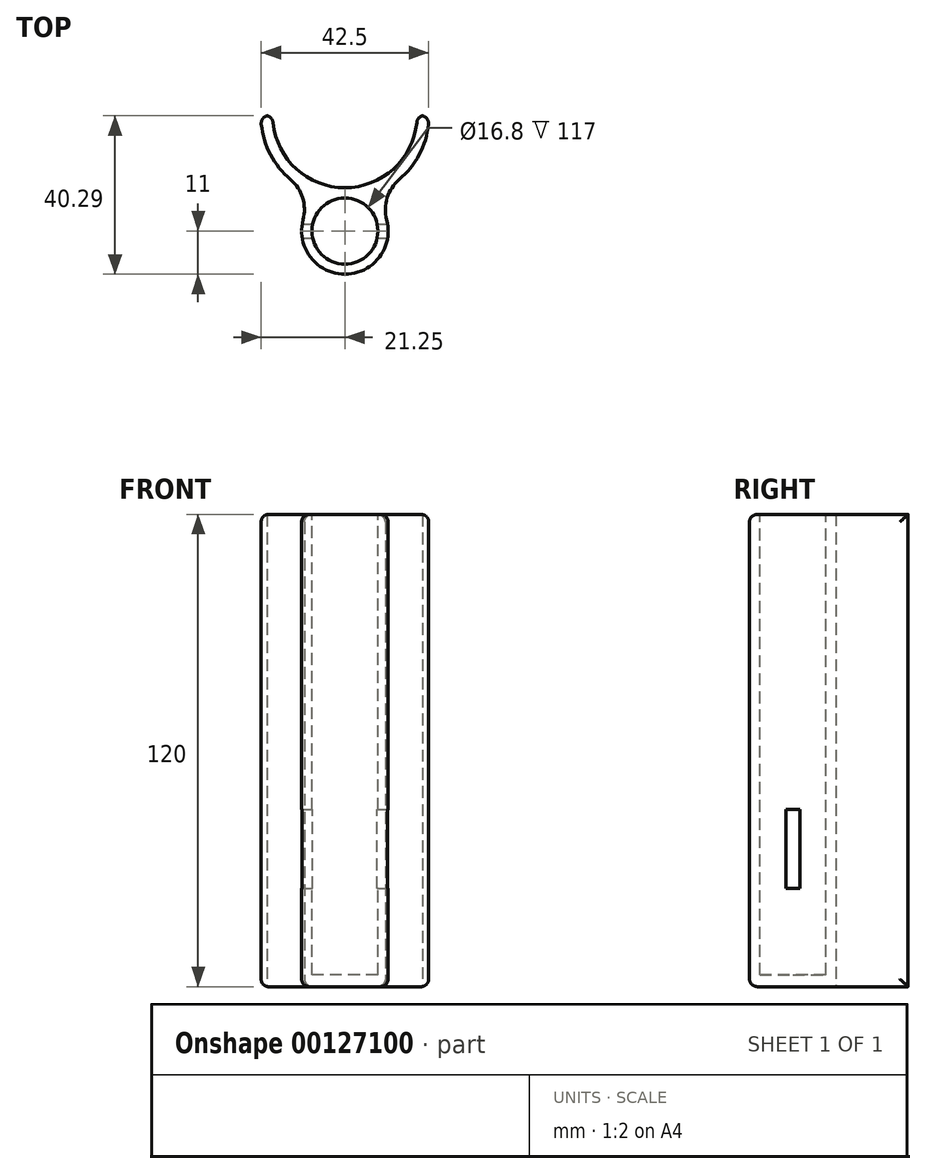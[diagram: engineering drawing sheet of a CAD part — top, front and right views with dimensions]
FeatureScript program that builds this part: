
annotation { "Feature Type Name" : "Feature", "Feature Type Description" : "" }
export const myFeature = defineFeature(function(context is Context, id is Id, definition is map)
    precondition{}
    {
        {
            var Q0;
            Q0=qCreatedBy(makeId("Top.planeOp"),FACE);
            var sketch = newSketch(context, id + "F0", { "sketchPlane" : qUnion([Q0])});
            skArc(sketch, "E0", {"start": v(-18.35, 0) * mm, "mid": v(0, -18.35) * mm, "end": v(18.35, 0) * mm});
            skArc(sketch, "E1.0", {"start": v(-21.35, 0) * mm, "mid": v(-19.37, -8.97) * mm, "end": v(-13.81, -16.28) * mm});
            skLineSegment(sketch, "E2", {"start": v(-21.35, 0) * mm, "end": v(-18.35, 0) * mm});
            skLineSegment(sketch, "E3.trimOffspring", {"start": v(18.35, 0) * mm, "end": v(21.35, 0) * mm});
            skPoint(sketch, "E4.orphan", {"position": v(-41.56, 0) * mm});
            skArc(sketch, "E5", {"start": v(-10.62, -26.5) * mm, "mid": v(0, -40.35) * mm, "end": v(10.62, -26.5) * mm});
            skPoint(sketch, "E5.centerSnap0", {"position": v(0, -21.35) * mm});
            skArc(sketch, "E6.trimOffspring", {"start": v(13.81, -16.28) * mm, "mid": v(19.37, -8.97) * mm, "end": v(21.35, 0) * mm});
            skPoint(sketch, "E7.visualSharp", {"position": v(-6.37, -20.38) * mm});
            skArc(sketch, "E7.filletArc", {"start": v(-10.62, -26.5) * mm, "mid": v(-10.74, -20.93) * mm, "end": v(-13.81, -16.28) * mm});
            skPoint(sketch, "E8.visualSharp", {"position": v(6.37, -20.38) * mm});
            skArc(sketch, "E8.filletArc", {"start": v(13.81, -16.28) * mm, "mid": v(10.74, -20.93) * mm, "end": v(10.62, -26.5) * mm});
            skSolve(sketch);
        }
        {
            var Q0;
            Q0 = qSketchRegion(id + "F0", true);
            extrude(context, id + "F1", {"entities" : qUnion([Q0]), "depth" : 120 * mm});
        }
        {
            var Q0;
            Q0=makeQuery(id+"F1.opExtrude","CAP_FACE",FACE,{"disambiguationData":[OSD([sQuery(id+"F0.wireOp",EDGE,"E0"),sQuery(id+"F0.wireOp",EDGE,"E1.0"),sQuery(id+"F0.wireOp",EDGE,"E2"),sQuery(id+"F0.wireOp",EDGE,"E3.trimOffspring"),sQuery(id+"F0.wireOp",EDGE,"E5"),sQuery(id+"F0.wireOp",EDGE,"E6.trimOffspring"),sQuery(id+"F0.wireOp",EDGE,"E7.filletArc"),sQuery(id+"F0.wireOp",EDGE,"E8.filletArc")])],"isStart":false});
            var sketch = newSketch(context, id + "F2", { "sketchPlane" : qUnion([Q0])});
            skCircle(sketch, "E9", {"center": v(0, -29.35) * mm, "radius": 8.4 * mm});
            skSolve(sketch);
        }
        {
            var Q0;
            Q0=makeQuery(id+"F2.imprint","IMPRINT",FACE,{"disambiguationData":[TD([[makeQuery(id+"F2.imprint","IMPRINT",EDGE,{"derivedFrom":sQuery(id+"F2.wireOp",EDGE,"E9")}),1.0]])]});
            extrude(context, id + "F3", {"entities" : qUnion([Q0]), "operationType" : NewBodyOperationType.REMOVE, "oppositeDirection" : true, "depth" : 117 * mm});
        }
        {
            var Q0;
            Q0=qCreatedBy(makeId("Top.planeOp"),FACE);
            var sketch = newSketch(context, id + "F4", { "sketchPlane" : qUnion([Q0])});
            skLineSegment(sketch, "E10.bottom", {"start": v(-16.23, -45.35) * mm, "end": v(20.53, -45.35) * mm});
            skLineSegment(sketch, "E10.top", {"start": v(-16.23, -48.85) * mm, "end": v(20.53, -48.85) * mm});
            skLineSegment(sketch, "E10.left", {"start": v(-16.23, -45.35) * mm, "end": v(-16.23, -48.85) * mm});
            skLineSegment(sketch, "E10.right", {"start": v(20.53, -45.35) * mm, "end": v(20.53, -48.85) * mm});
            skSolve(sketch);
        }
        {
            var Q0;
            Q0=makeQuery(id+"F4.imprint","IMPRINT",FACE,{"disambiguationData":[TD([[makeQuery(id+"F4.imprint","IMPRINT",EDGE,{"derivedFrom":sQuery(id+"F4.wireOp",EDGE,"E10.bottom")}),-1.0]])]});
            extrude(context, id + "F5", {"entities" : qUnion([Q0]), "depth" : 20 * mm});
        }
        {
            var Q0;
            Q0=makeQuery(id+"F5.opExtrude","SWEPT_BODY",BODY,{"disambiguationData":[OSD([sQuery(id+"F4.wireOp",EDGE,"E10.bottom"),sQuery(id+"F4.wireOp",EDGE,"E10.top"),sQuery(id+"F4.wireOp",EDGE,"E10.left"),sQuery(id+"F4.wireOp",EDGE,"E10.right")])]});
            transform(context, id + "F6", {"entities" : qUnion([Q0]), "transformType" : TransformType.TRANSLATION_3D, "dx" : 0 * mm, "dy" : 17.75 * mm, "dz" : 25 * mm, "makeCopy" : false});
        }
        {
            var Q0;
            Q0=makeQuery(id+"F5.opExtrude","SWEPT_BODY",BODY,{"disambiguationData":[OSD([sQuery(id+"F4.wireOp",EDGE,"E10.bottom"),sQuery(id+"F4.wireOp",EDGE,"E10.top"),sQuery(id+"F4.wireOp",EDGE,"E10.left"),sQuery(id+"F4.wireOp",EDGE,"E10.right")])]});
            var Q1;
            Q1=makeQuery(id+"F1.opExtrude","SWEPT_BODY",BODY,{"disambiguationData":[OSD([sQuery(id+"F0.wireOp",EDGE,"E0"),sQuery(id+"F0.wireOp",EDGE,"E1.0"),sQuery(id+"F0.wireOp",EDGE,"E2"),sQuery(id+"F0.wireOp",EDGE,"E3.trimOffspring"),sQuery(id+"F0.wireOp",EDGE,"E5"),sQuery(id+"F0.wireOp",EDGE,"E6.trimOffspring"),sQuery(id+"F0.wireOp",EDGE,"E7.filletArc"),sQuery(id+"F0.wireOp",EDGE,"E8.filletArc")])]});
            booleanBodies(context, id + "F7", {"operationType" : BooleanOperationType.SUBTRACTION, "tools" : qUnion([Q0]), "targets" : qUnion([Q1])});
        }
        {
            var Q0;
            Q0=qCreatedBy(makeId("Top.planeOp"),FACE);
            var sketch = newSketch(context, id + "F8", { "sketchPlane" : qUnion([Q0])});
            skCircle(sketch, "E11", {"center": v(47.17, -35.85) * mm, "radius": 8 * mm});
            skSolve(sketch);
        }
        {
            var Q0;
            Q0 = qSketchRegion(id + "F8", true);
            extrude(context, id + "F9", {"entities" : qUnion([Q0]), "depth" : 75 * mm});
        }
        {
            var Q0;
            Q0=makeQuery(id+"F9.opExtrude","CAP_FACE",FACE,{"disambiguationData":[OSD([sQuery(id+"F8.wireOp",EDGE,"E11")])],"isStart":false});
            var sketch = newSketch(context, id + "F10", { "sketchPlane" : qUnion([Q0])});
            skCircle(sketch, "E12", {"center": v(47.17, -35.85) * mm, "radius": 5.1 * mm});
            skSolve(sketch);
        }
        {
            var Q0;
            Q0 = qSketchRegion(id + "F10", true);
            extrude(context, id + "F11", {"entities" : qUnion([Q0]), "operationType" : NewBodyOperationType.REMOVE, "oppositeDirection" : true, "depth" : 72 * mm});
        }
        {
            var Q0;
            Q0=makeQuery(id+"F1.opExtrude","SWEPT_EDGE",EDGE,{"disambiguationData":[OSD([sQuery(id+"F0.wireOp",EDGE,"E1.0"),sQuery(id+"F0.wireOp",EDGE,"E2")])]});
            var Q1;
            Q1=makeQuery(id+"F1.opExtrude","SWEPT_EDGE",EDGE,{"disambiguationData":[OSD([sQuery(id+"F0.wireOp",EDGE,"E0"),sQuery(id+"F0.wireOp",EDGE,"E2")])]});
            var Q2;
            Q2=makeQuery(id+"F1.opExtrude","SWEPT_EDGE",EDGE,{"disambiguationData":[OSD([sQuery(id+"F0.wireOp",EDGE,"E0"),sQuery(id+"F0.wireOp",EDGE,"E3.trimOffspring")])]});
            var Q3;
            Q3=makeQuery(id+"F1.opExtrude","SWEPT_EDGE",EDGE,{"disambiguationData":[OSD([sQuery(id+"F0.wireOp",EDGE,"E3.trimOffspring"),sQuery(id+"F0.wireOp",EDGE,"E6.trimOffspring")])]});
            var Q4;
            Q4=makeQuery(id+"F1.opExtrude","CAP_EDGE",EDGE,{"disambiguationData":[OSD([sQuery(id+"F0.wireOp",EDGE,"E5")])],"isStart":false});
            var Q5;
            Q5=makeQuery(id+"F1.opExtrude","CAP_EDGE",EDGE,{"disambiguationData":[OSD([sQuery(id+"F0.wireOp",EDGE,"E1.0")])],"isStart":true});
            fillet(context, id + "F12", {"entities" : qUnion([Q0, Q1, Q2, Q3, Q4, Q5]), "radius" : 2 * mm, "tangentPropagation" : true, "allowEdgeOverflow" : false});
        }
        {
            var Q0;
            Q0=makeQuery(id+"F9.opExtrude","SWEPT_BODY",BODY,{"disambiguationData":[OSD([sQuery(id+"F8.wireOp",EDGE,"E11")])]});
            deleteBodies(context, id + "F13", {"entities" : qUnion([Q0])});
        }
    });
